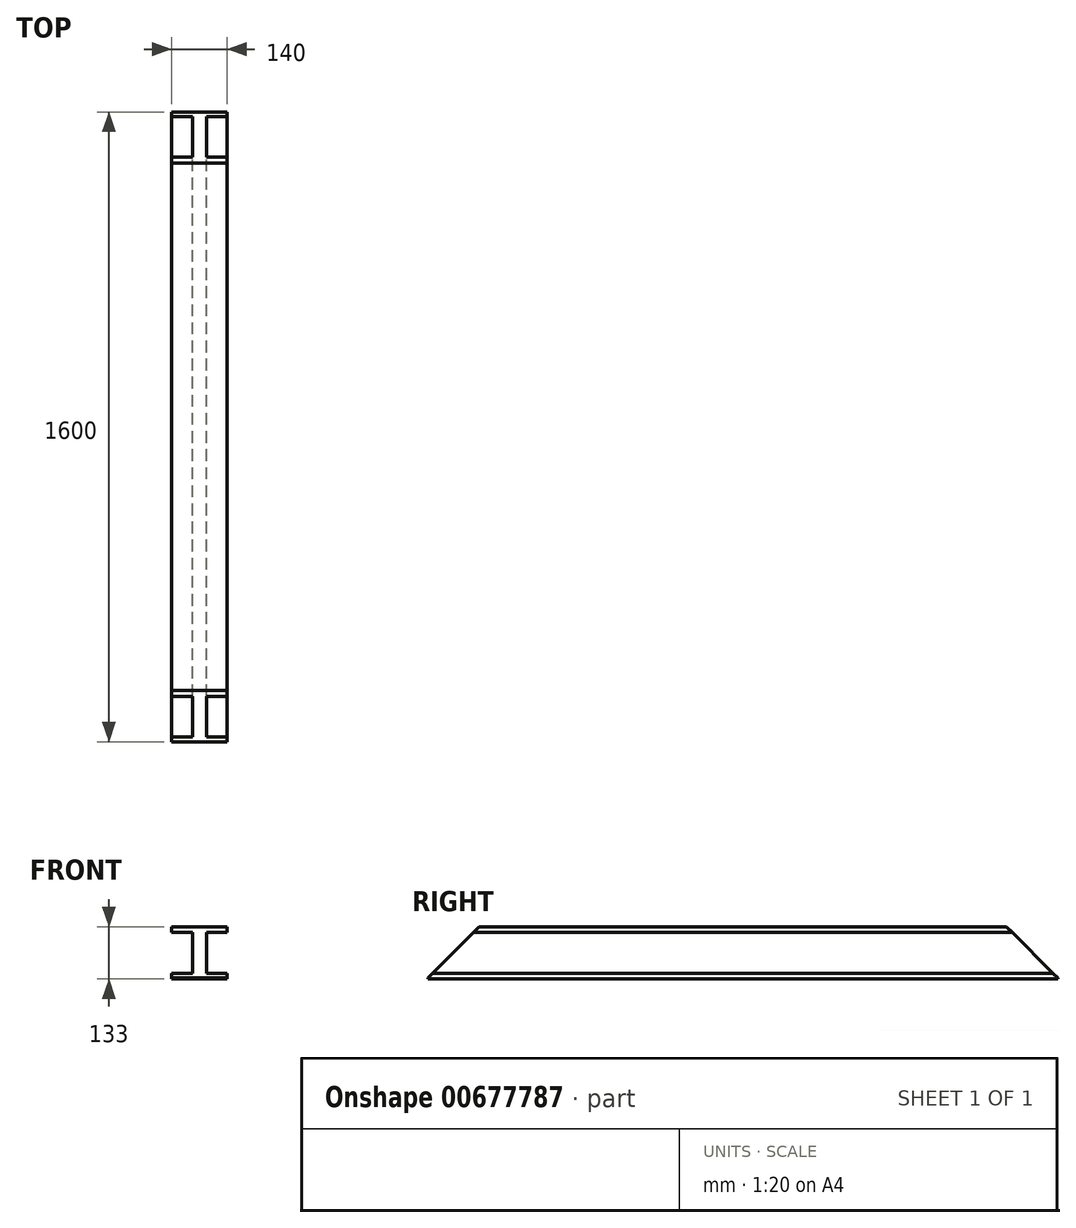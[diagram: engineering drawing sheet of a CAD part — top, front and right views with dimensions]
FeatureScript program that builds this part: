
annotation { "Feature Type Name" : "Feature", "Feature Type Description" : "" }
export const myFeature = defineFeature(function(context is Context, id is Id, definition is map)
    precondition{}
    {
        {
            var Q0;
            Q0=qCreatedBy(makeId("Front.planeOp"),FACE);
            var sketch = newSketch(context, id + "F0", { "sketchPlane" : qUnion([Q0])});
            skLineSegment(sketch, "E0.bottom", {"start": v(70, -66.5) * mm, "end": v(-70, -66.5) * mm});
            skLineSegment(sketch, "E0.top", {"start": v(70, 66.5) * mm, "end": v(-70, 66.5) * mm});
            skLineSegment(sketch, "E0.left", {"start": v(70, -66.5) * mm, "end": v(70, -51.75) * mm});
            skLineSegment(sketch, "E0.right", {"start": v(-70, -66.5) * mm, "end": v(-70, -51.75) * mm});
            skPoint(sketch, "E0.middle", {"position": v(0, 0) * mm});
            skLineSegment(sketch, "E1", {"start": v(0, 66.5) * mm, "end": v(0, -108.78) * mm, "construction": true});
            skLineSegment(sketch, "E2.bottom", {"start": v(70, -51.75) * mm, "end": v(17.64, -51.75) * mm});
            skLineSegment(sketch, "E2.top", {"start": v(70, 51.75) * mm, "end": v(17.64, 51.75) * mm});
            skLineSegment(sketch, "E2.right", {"start": v(17.64, -51.75) * mm, "end": v(17.64, 51.75) * mm});
            skLineSegment(sketch, "E3.trimOffspring", {"start": v(70, 51.75) * mm, "end": v(70, 66.5) * mm});
            skLineSegment(sketch, "E4.MirrorCS", {"start": v(-70, 51.75) * mm, "end": v(-17.64, 51.75) * mm});
            skLineSegment(sketch, "E5.MirrorCS", {"start": v(-17.64, -51.75) * mm, "end": v(-17.64, 51.75) * mm});
            skLineSegment(sketch, "E6.MirrorCS", {"start": v(-70, -51.75) * mm, "end": v(-17.64, -51.75) * mm});
            skLineSegment(sketch, "E7.trimOffspring", {"start": v(-70, 51.75) * mm, "end": v(-70, 66.5) * mm});
            skSolve(sketch);
        }
        {
            var Q0;
            Q0 = qSketchRegion(id + "F0", true);
            extrude(context, id + "F1", {"entities" : qUnion([Q0]), "depth" : 1600 * mm, "offsetDistance" : 25 * mm});
        }
        {
            var Q0;
            Q0=makeQuery(id+"F1.opExtrude","CAP_EDGE",EDGE,{"disambiguationData":[OSD([sQuery(id+"F0.wireOp",EDGE,"E0.top")])],"isStart":false});
            var Q1;
            Q1=makeQuery(id+"F1.opExtrude","CAP_EDGE",EDGE,{"disambiguationData":[OSD([sQuery(id+"F0.wireOp",EDGE,"E0.top")])],"isStart":true});
            chamfer(context, id + "F2", {"entities" : qUnion([Q0, Q1]), "width" : 130 * mm, "tangentPropagation" : true});
        }
    });
